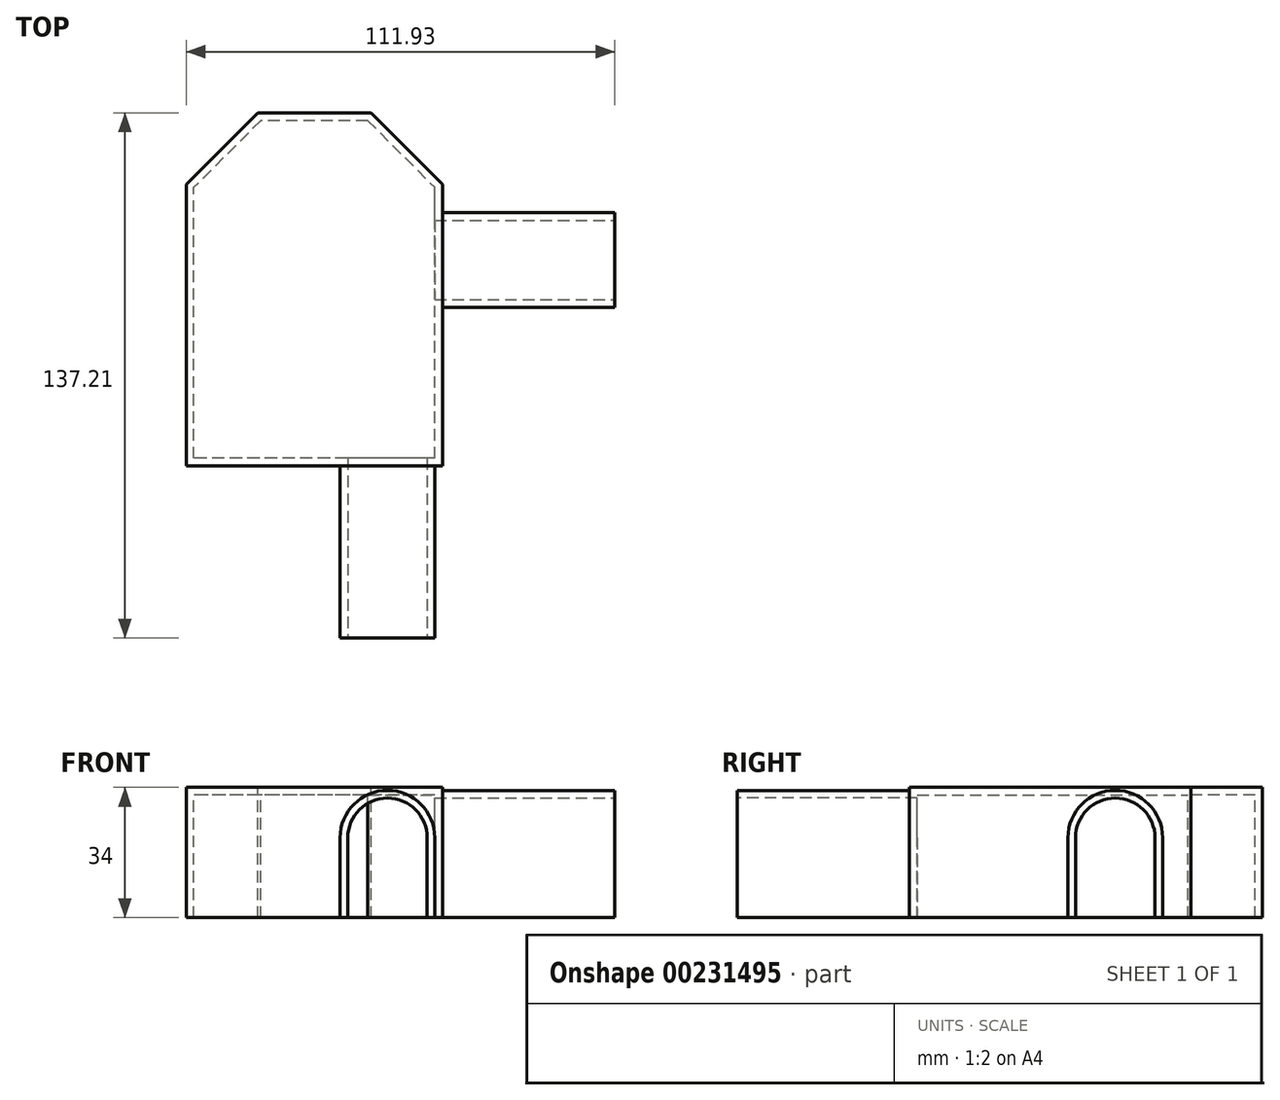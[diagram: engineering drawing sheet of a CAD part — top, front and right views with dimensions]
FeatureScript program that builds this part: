
annotation { "Feature Type Name" : "Feature", "Feature Type Description" : "" }
export const myFeature = defineFeature(function(context is Context, id is Id, definition is map)
    precondition{}
    {
        {
            var Q0;
            Q0=qCreatedBy(makeId("Top.planeOp"),FACE);
            var sketch = newSketch(context, id + "F0", { "sketchPlane" : qUnion([Q0])});
            skLineSegment(sketch, "E0.bottom", {"start": v(0, 0) * mm, "end": v(-62.93, 0) * mm});
            skLineSegment(sketch, "E0.top", {"start": v(-17.5, 88.2) * mm, "end": v(-45.43, 88.2) * mm});
            skLineSegment(sketch, "E0.left", {"start": v(0, 0) * mm, "end": v(0, 70.7) * mm});
            skLineSegment(sketch, "E0.right", {"start": v(-62.93, 0) * mm, "end": v(-62.93, 70.7) * mm});
            skLineSegment(sketch, "E1", {"start": v(-45.43, 88.2) * mm, "end": v(-62.93, 70.7) * mm});
            skLineSegment(sketch, "E2", {"start": v(-17.5, 88.2) * mm, "end": v(0, 70.7) * mm});
            skLineSegment(sketch, "E3.0", {"start": v(-16.67, 90.2) * mm, "end": v(-46.26, 90.2) * mm});
            skLineSegment(sketch, "E3.1", {"start": v(-64.93, -2) * mm, "end": v(-64.93, 71.54) * mm});
            skLineSegment(sketch, "E3.2", {"start": v(2, -2) * mm, "end": v(-64.93, -2) * mm});
            skLineSegment(sketch, "E3.3", {"start": v(-46.26, 90.2) * mm, "end": v(-64.93, 71.54) * mm});
            skLineSegment(sketch, "E3.4", {"start": v(2, -2) * mm, "end": v(2, 71.54) * mm});
            skLineSegment(sketch, "E3.5", {"start": v(-16.67, 90.2) * mm, "end": v(2, 71.54) * mm});
            skSolve(sketch);
        }
        {
            var Q0;
            Q0=makeQuery(id+"F0.imprint","IMPRINT",FACE,{"disambiguationData":[TD([[makeQuery(id+"F0.imprint","IMPRINT",EDGE,{"derivedFrom":sQuery(id+"F0.wireOp",EDGE,"E0.bottom")}),1.0]])]});
            extrude(context, id + "F1", {"entities" : qUnion([Q0]), "oppositeDirection" : true, "depth" : 32 * mm});
        }
        {
            var Q0;
            Q0=makeQuery(id+"F1.opExtrude","CAP_FACE",FACE,{"disambiguationData":[OSD([sQuery(id+"F0.wireOp",EDGE,"E0.bottom"),sQuery(id+"F0.wireOp",EDGE,"E0.top"),sQuery(id+"F0.wireOp",EDGE,"E0.left"),sQuery(id+"F0.wireOp",EDGE,"E0.right"),sQuery(id+"F0.wireOp",EDGE,"E1"),sQuery(id+"F0.wireOp",EDGE,"E2"),sQuery(id+"F0.wireOp",EDGE,"E3.0"),sQuery(id+"F0.wireOp",EDGE,"E3.1"),sQuery(id+"F0.wireOp",EDGE,"E3.2"),sQuery(id+"F0.wireOp",EDGE,"E3.3"),sQuery(id+"F0.wireOp",EDGE,"E3.4"),sQuery(id+"F0.wireOp",EDGE,"E3.5")])],"isStart":true});
            var sketch = newSketch(context, id + "F2", { "sketchPlane" : qUnion([Q0])});
            skLineSegment(sketch, "E4", {"start": v(-64.93, -2) * mm, "end": v(2, -2) * mm});
            skLineSegment(sketch, "E5", {"start": v(2, -2) * mm, "end": v(2, 71.54) * mm});
            skLineSegment(sketch, "E6", {"start": v(2, 71.54) * mm, "end": v(-16.67, 90.2) * mm});
            skLineSegment(sketch, "E7", {"start": v(-16.67, 90.2) * mm, "end": v(-46.26, 90.2) * mm});
            skLineSegment(sketch, "E8", {"start": v(-46.26, 90.2) * mm, "end": v(-64.93, 71.54) * mm});
            skLineSegment(sketch, "E9", {"start": v(-64.93, 71.54) * mm, "end": v(-64.93, -2) * mm});
            skSolve(sketch);
        }
        {
            var Q0;
            Q0 = qSketchRegion(id + "F2", true);
            extrude(context, id + "F3", {"entities" : qUnion([Q0]), "operationType" : NewBodyOperationType.ADD, "depth" : 2 * mm});
        }
        {
            var Q0;
            Q0=makeQuery(id+"F3.boolean.opBoolean","MERGE",FACE,{"derivedFrom":[makeQuery(id+"F1.opExtrude","SWEPT_FACE",FACE,{"disambiguationData":[OSD([sQuery(id+"F0.wireOp",EDGE,"E3.2")])]}),makeQuery(id+"F3.opExtrude","SWEPT_FACE",FACE,{"disambiguationData":[OSD([sQuery(id+"F2.wireOp",EDGE,"E4")])]})]});
            var sketch = newSketch(context, id + "F4", { "sketchPlane" : qUnion([Q0])});
            skLineSegment(sketch, "E10", {"start": v(-22.73, -11.15) * mm, "end": v(-22.73, -32) * mm});
            skLineSegment(sketch, "E11", {"start": v(-1.98, -11.15) * mm, "end": v(-1.98, -32) * mm});
            skLineSegment(sketch, "E12", {"start": v(-1.98, -32) * mm, "end": v(-22.73, -32) * mm});
            skArc(sketch, "E13", {"start": v(-22.73, -11.15) * mm, "mid": v(-19.7, -3.82) * mm, "end": v(-12.35, -0.78) * mm});
            skArc(sketch, "E14", {"start": v(-1.98, -11.15) * mm, "mid": v(-5.02, -3.82) * mm, "end": v(-12.35, -0.78) * mm});
            skSolve(sketch);
        }
        {
            var Q0;
            Q0=makeQuery(id+"F4.imprint","IMPRINT",FACE,{"disambiguationData":[TD([[makeQuery(id+"F4.imprint","IMPRINT",EDGE,{"derivedFrom":sQuery(id+"F4.wireOp",EDGE,"E10")}),1.0]])]});
            extrude(context, id + "F5", {"entities" : qUnion([Q0]), "operationType" : NewBodyOperationType.REMOVE, "oppositeDirection" : true, "depth" : 2 * mm});
        }
        {
            var Q0;
            Q0=makeQuery(id+"F3.boolean.opBoolean","MERGE",FACE,{"derivedFrom":[makeQuery(id+"F1.opExtrude","SWEPT_FACE",FACE,{"disambiguationData":[OSD([sQuery(id+"F0.wireOp",EDGE,"E3.4")])]}),makeQuery(id+"F3.opExtrude","SWEPT_FACE",FACE,{"disambiguationData":[OSD([sQuery(id+"F2.wireOp",EDGE,"E5")])]})]});
            var sketch = newSketch(context, id + "F6", { "sketchPlane" : qUnion([Q0])});
            skLineSegment(sketch, "E15", {"start": v(62.13, -11.16) * mm, "end": v(62.13, -32) * mm});
            skLineSegment(sketch, "E16", {"start": v(41.37, -11.16) * mm, "end": v(41.37, -32) * mm});
            skLineSegment(sketch, "E17", {"start": v(41.37, -32) * mm, "end": v(62.13, -32) * mm});
            skArc(sketch, "E18", {"start": v(41.38, -11.16) * mm, "mid": v(44.41, -3.82) * mm, "end": v(51.75, -0.78) * mm});
            skArc(sketch, "E19", {"start": v(62.13, -11.16) * mm, "mid": v(59.09, -3.82) * mm, "end": v(51.75, -0.78) * mm});
            skSolve(sketch);
        }
        {
            var Q0;
            Q0=makeQuery(id+"F6.imprint","IMPRINT",FACE,{"disambiguationData":[TD([[makeQuery(id+"F6.imprint","IMPRINT",EDGE,{"derivedFrom":sQuery(id+"F6.wireOp",EDGE,"E15")}),-1.0]])]});
            extrude(context, id + "F7", {"entities" : qUnion([Q0]), "operationType" : NewBodyOperationType.REMOVE, "oppositeDirection" : true, "depth" : 2 * mm});
        }
        {
            var Q0;
            Q0=makeQuery(id+"F3.boolean.opBoolean","MERGE",FACE,{"derivedFrom":[makeQuery(id+"F1.opExtrude","SWEPT_FACE",FACE,{"disambiguationData":[OSD([sQuery(id+"F0.wireOp",EDGE,"E3.2")])]}),makeQuery(id+"F3.opExtrude","SWEPT_FACE",FACE,{"disambiguationData":[OSD([sQuery(id+"F2.wireOp",EDGE,"E4")])]})]});
            var sketch = newSketch(context, id + "F8", { "sketchPlane" : qUnion([Q0])});
            skLineSegment(sketch, "E20.0", {"start": v(-24.73, -11.15) * mm, "end": v(-24.73, -32) * mm});
            skArc(sketch, "E20.1", {"start": v(0.02, -11.15) * mm, "mid": v(-12.35, 1.22) * mm, "end": v(-24.73, -11.15) * mm});
            skLineSegment(sketch, "E20.2", {"start": v(0.02, -11.15) * mm, "end": v(0.02, -32) * mm});
            skLineSegment(sketch, "E21", {"start": v(-24.73, -32) * mm, "end": v(-22.73, -32) * mm});
            skLineSegment(sketch, "E22", {"start": v(0.02, -32) * mm, "end": v(-1.98, -32) * mm});
            skSolve(sketch);
        }
        {
            var Q0;
            Q0=makeQuery(id+"F8.imprint","IMPRINT",FACE,{"disambiguationData":[TD([[makeQuery(id+"F8.imprint","IMPRINT",EDGE,{"derivedFrom":sQuery(id+"F8.wireOp",EDGE,"E20.0")}),1.0]])]});
            extrude(context, id + "F9", {"entities" : qUnion([Q0]), "operationType" : NewBodyOperationType.ADD, "depth" : 45 * mm});
        }
        {
            var Q0;
            Q0=makeQuery(id+"F3.boolean.opBoolean","MERGE",FACE,{"derivedFrom":[makeQuery(id+"F1.opExtrude","SWEPT_FACE",FACE,{"disambiguationData":[OSD([sQuery(id+"F0.wireOp",EDGE,"E3.4")])]}),makeQuery(id+"F3.opExtrude","SWEPT_FACE",FACE,{"disambiguationData":[OSD([sQuery(id+"F2.wireOp",EDGE,"E5")])]})]});
            var sketch = newSketch(context, id + "F10", { "sketchPlane" : qUnion([Q0])});
            skLineSegment(sketch, "E23.0", {"start": v(39.37, -11.16) * mm, "end": v(39.37, -32) * mm});
            skArc(sketch, "E23.1", {"start": v(39.38, -11.16) * mm, "mid": v(51.75, 1.22) * mm, "end": v(64.13, -11.16) * mm});
            skLineSegment(sketch, "E23.2", {"start": v(64.13, -11.16) * mm, "end": v(64.13, -32) * mm});
            skLineSegment(sketch, "E24", {"start": v(39.37, -32) * mm, "end": v(41.37, -32) * mm});
            skLineSegment(sketch, "E25", {"start": v(64.13, -32) * mm, "end": v(62.13, -32) * mm});
            skSolve(sketch);
        }
        {
            var Q0;
            Q0=makeQuery(id+"F10.imprint","IMPRINT",FACE,{"disambiguationData":[TD([[makeQuery(id+"F10.imprint","IMPRINT",EDGE,{"derivedFrom":sQuery(id+"F10.wireOp",EDGE,"E23.0")}),1.0]])]});
            extrude(context, id + "F11", {"entities" : qUnion([Q0]), "operationType" : NewBodyOperationType.ADD, "depth" : 45 * mm});
        }
    });
